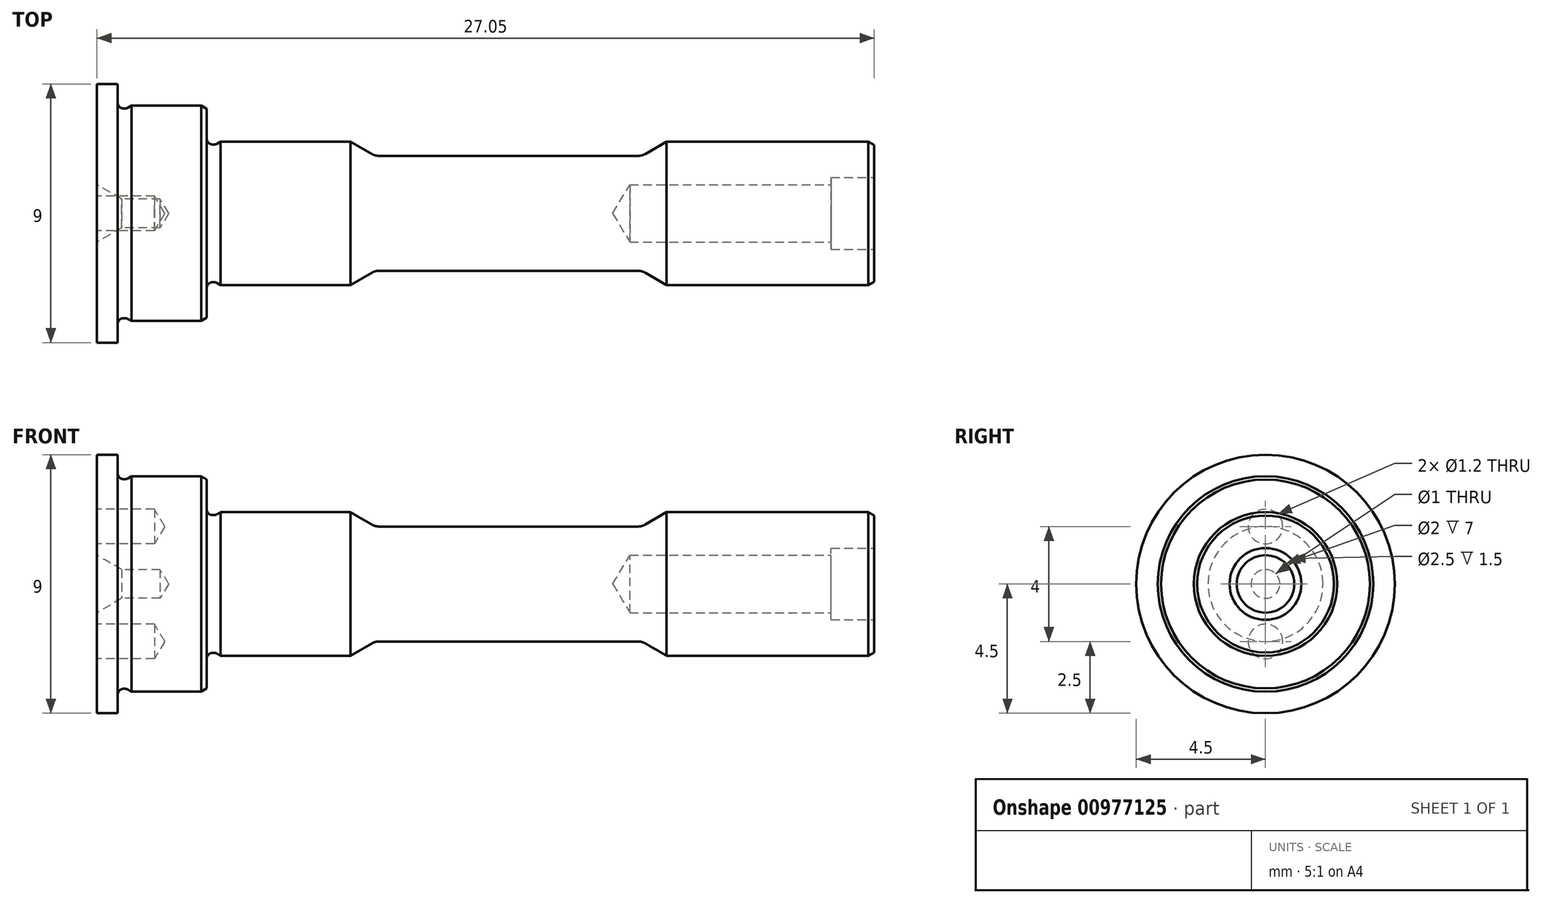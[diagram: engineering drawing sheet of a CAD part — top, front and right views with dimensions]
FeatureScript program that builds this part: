
annotation { "Feature Type Name" : "Feature", "Feature Type Description" : "" }
export const myFeature = defineFeature(function(context is Context, id is Id, definition is map)
    precondition{}
    {
        {
            var Q0;
            Q0=qCreatedBy(makeId("Front.planeOp"),FACE);
            var sketch = newSketch(context, id + "F0", { "sketchPlane" : qUnion([Q0])});
            skLineSegment(sketch, "E0", {"start": v(0, 0) * mm, "end": v(0, 4.5) * mm});
            skLineSegment(sketch, "E1", {"start": v(3.82, 3.75) * mm, "end": v(3.82, 2.6) * mm});
            skArc(sketch, "E2", {"start": v(3.82, 2.6) * mm, "mid": v(3.88, 2.45) * mm, "end": v(4.02, 2.4) * mm});
            skLineSegment(sketch, "E3", {"start": v(4.02, 2.4) * mm, "end": v(4.08, 2.4) * mm});
            skArc(sketch, "E4", {"start": v(4.08, 2.4) * mm, "mid": v(4.13, 2.4) * mm, "end": v(4.18, 2.42) * mm});
            skLineSegment(sketch, "E5", {"start": v(4.18, 2.42) * mm, "end": v(4.3, 2.5) * mm});
            skLineSegment(sketch, "E6", {"start": v(4.3, 2.5) * mm, "end": v(27.05, 2.5) * mm});
            skLineSegment(sketch, "E7", {"start": v(27.05, 2.5) * mm, "end": v(27.05, 0) * mm});
            skLineSegment(sketch, "E8", {"start": v(27.05, 0) * mm, "end": v(0, 0) * mm});
            skLineSegment(sketch, "E9", {"start": v(0, 4.5) * mm, "end": v(0.72, 4.5) * mm});
            skLineSegment(sketch, "E10", {"start": v(0.72, 4.5) * mm, "end": v(0.72, 3.85) * mm});
            skLineSegment(sketch, "E11", {"start": v(1.2, 3.75) * mm, "end": v(3.82, 3.75) * mm});
            skLineSegment(sketch, "E12", {"start": v(1.2, 3.75) * mm, "end": v(1.08, 3.68) * mm});
            skLineSegment(sketch, "E13", {"start": v(0.98, 3.65) * mm, "end": v(0.92, 3.65) * mm});
            skPoint(sketch, "E14.visualSharp", {"position": v(0.72, 3.65) * mm});
            skArc(sketch, "E14.filletArc", {"start": v(0.72, 3.85) * mm, "mid": v(0.78, 3.7) * mm, "end": v(0.92, 3.65) * mm});
            skPoint(sketch, "E15.visualSharp", {"position": v(1.03, 3.65) * mm});
            skArc(sketch, "E15.filletArc", {"start": v(0.98, 3.65) * mm, "mid": v(1.03, 3.66) * mm, "end": v(1.08, 3.68) * mm});
            skLineSegment(sketch, "E16", {"start": v(8.82, 2.5) * mm, "end": v(9.68, 2) * mm});
            skLineSegment(sketch, "E17", {"start": v(9.68, 2) * mm, "end": v(18.97, 2) * mm});
            skLineSegment(sketch, "E18", {"start": v(18.97, 2) * mm, "end": v(19.83, 2.5) * mm});
            skLineSegment(sketch, "E19", {"start": v(19.83, 2.5) * mm, "end": v(8.82, 2.5) * mm});
            skSolve(sketch);
        }
        {
            var Q0;
            Q0=makeQuery(id+"F0.imprint","IMPRINT",FACE,{"disambiguationData":[TD([[makeQuery(id+"F0.imprint","IMPRINT",EDGE,{"derivedFrom":sQuery(id+"F0.wireOp",EDGE,"E0")}),-1.0]])]});
            var Q1;
            Q1=sQuery(id+"F0.wireOp",EDGE,"E8");
            revolve(context, id + "F1", {"surfaceOperationType" : NewSurfaceOperationType.NEW, "entities" : qUnion([Q0]), "axis" : qUnion([Q1]), "revolveType" : RevolveType.FULL});
        }
        {
            var Q0;
            Q0=makeQuery(id+"F1.opRevolve","SWEPT_EDGE",EDGE,{"disambiguationData":[OSD([sQuery(id+"F0.wireOp",EDGE,"E16"),sQuery(id+"F0.wireOp",EDGE,"E17")])]});
            var Q1;
            Q1=makeQuery(id+"F1.opRevolve","SWEPT_EDGE",EDGE,{"disambiguationData":[OSD([sQuery(id+"F0.wireOp",EDGE,"E17"),sQuery(id+"F0.wireOp",EDGE,"E18")])]});
            fillet(context, id + "F2", {"entities" : qUnion([Q0, Q1]), "tangentPropagation" : true, "radius" : .5 * mm, "defaultsChanged" : true, "vertexSettings" : [], "allowEdgeOverflow" : false});
        }
        {
            var Q0;
            Q0=makeQuery(id+"F1.opRevolve","SWEPT_EDGE",EDGE,{"disambiguationData":[OSD([sQuery(id+"F0.wireOp",EDGE,"E1"),sQuery(id+"F0.wireOp",EDGE,"E11")])]});
            var Q1;
            Q1=makeQuery(id+"F1.opRevolve","SWEPT_EDGE",EDGE,{"disambiguationData":[OSD([sQuery(id+"F0.wireOp",EDGE,"E6"),sQuery(id+"F0.wireOp",EDGE,"E7")])]});
            chamfer(context, id + "F3", {"entities" : qUnion([Q0, Q1]), "chamferType" : ChamferType.OFFSET_ANGLE, "width" : .2 * mm, "oppositeDirection" : true, "angle" : 30 * degree, "tangentPropagation" : true});
        }
        {
            var Q0;
            Q0=makeQuery(id+"F1.opRevolve","SWEPT_FACE",FACE,{"disambiguationData":[OSD([sQuery(id+"F0.wireOp",EDGE,"E7")])]});
            var sketch = newSketch(context, id + "F4", { "sketchPlane" : qUnion([Q0])});
            skPoint(sketch, "E20", {"position": v(0, 0) * mm});
            skSolve(sketch);
        }
        {
            var Q0;
            Q0=makeQuery(id+"F1.opRevolve","SWEPT_FACE",FACE,{"disambiguationData":[OSD([sQuery(id+"F0.wireOp",EDGE,"E0")])]});
            var sketch = newSketch(context, id + "F5", { "sketchPlane" : qUnion([Q0])});
            skPoint(sketch, "E21", {"position": v(0, 0) * mm});
            skPoint(sketch, "E22", {"position": v(0, 2) * mm});
            skPoint(sketch, "E23", {"position": v(0, -2) * mm});
            skSolve(sketch);
        }
        {
            var Q0;
            Q0=sQuery(id+"F5.wireOp",VERTEX,"E22");
            var Q1;
            Q1=sQuery(id+"F5.wireOp",VERTEX,"E23");
            var Q2;
            Q2=makeQuery(id+"F1.opRevolve","SWEPT_BODY",BODY,{"disambiguationData":[OSD([sQuery(id+"F0.wireOp",EDGE,"E0"),sQuery(id+"F0.wireOp",EDGE,"E1"),sQuery(id+"F0.wireOp",EDGE,"E2"),sQuery(id+"F0.wireOp",EDGE,"E3"),sQuery(id+"F0.wireOp",EDGE,"E4"),sQuery(id+"F0.wireOp",EDGE,"E5"),sQuery(id+"F0.wireOp",EDGE,"E6"),sQuery(id+"F0.wireOp",EDGE,"E7"),sQuery(id+"F0.wireOp",EDGE,"E8"),sQuery(id+"F0.wireOp",EDGE,"E9"),sQuery(id+"F0.wireOp",EDGE,"E10"),sQuery(id+"F0.wireOp",EDGE,"E11"),sQuery(id+"F0.wireOp",EDGE,"E12"),sQuery(id+"F0.wireOp",EDGE,"E13"),sQuery(id+"F0.wireOp",EDGE,"E14.filletArc"),sQuery(id+"F0.wireOp",EDGE,"E15.filletArc"),sQuery(id+"F0.wireOp",EDGE,"E16"),sQuery(id+"F0.wireOp",EDGE,"E17"),sQuery(id+"F0.wireOp",EDGE,"E18")])]});
            hole(context, id + "F6", {"style" : HoleStyle.SIMPLE, "endStyle" : HoleEndStyle.BLIND, "holeDiameter" : 1.2 * mm, "majorDiameter" : 5 * mm, "holeDepth" : 2 * mm, "isTappedThrough" : true, "tappedDepth" : 12 * mm, "tapClearance" : 3, "locations" : qUnion([Q0, Q1]), "scope" : qUnion([Q2])});
        }
        {
            var Q0;
            Q0=sQuery(id+"F5.wireOp",VERTEX,"E21");
            var Q1;
            Q1=makeQuery(id+"F1.opRevolve","SWEPT_BODY",BODY,{"disambiguationData":[OSD([sQuery(id+"F0.wireOp",EDGE,"E0"),sQuery(id+"F0.wireOp",EDGE,"E1"),sQuery(id+"F0.wireOp",EDGE,"E2"),sQuery(id+"F0.wireOp",EDGE,"E3"),sQuery(id+"F0.wireOp",EDGE,"E4"),sQuery(id+"F0.wireOp",EDGE,"E5"),sQuery(id+"F0.wireOp",EDGE,"E6"),sQuery(id+"F0.wireOp",EDGE,"E7"),sQuery(id+"F0.wireOp",EDGE,"E8"),sQuery(id+"F0.wireOp",EDGE,"E9"),sQuery(id+"F0.wireOp",EDGE,"E10"),sQuery(id+"F0.wireOp",EDGE,"E11"),sQuery(id+"F0.wireOp",EDGE,"E12"),sQuery(id+"F0.wireOp",EDGE,"E13"),sQuery(id+"F0.wireOp",EDGE,"E14.filletArc"),sQuery(id+"F0.wireOp",EDGE,"E15.filletArc"),sQuery(id+"F0.wireOp",EDGE,"E16"),sQuery(id+"F0.wireOp",EDGE,"E17"),sQuery(id+"F0.wireOp",EDGE,"E18")])]});
            hole(context, id + "F7", {"style" : HoleStyle.C_SINK, "endStyle" : HoleEndStyle.BLIND, "holeDiameter" : 1 * mm, "cSinkDiameter" : 2 * mm, "cSinkAngle" : 60 * degree, "majorDiameter" : 5 * mm, "holeDepth" : 2.2 * mm, "isTappedThrough" : true, "tappedDepth" : 12 * mm, "tapClearance" : 3, "locations" : qUnion([Q0]), "scope" : qUnion([Q1])});
        }
        {
            var Q0;
            Q0=sQuery(id+"F4.wireOp",VERTEX,"E20");
            var Q1;
            Q1=makeQuery(id+"F1.opRevolve","SWEPT_BODY",BODY,{"disambiguationData":[OSD([sQuery(id+"F0.wireOp",EDGE,"E0"),sQuery(id+"F0.wireOp",EDGE,"E1"),sQuery(id+"F0.wireOp",EDGE,"E2"),sQuery(id+"F0.wireOp",EDGE,"E3"),sQuery(id+"F0.wireOp",EDGE,"E4"),sQuery(id+"F0.wireOp",EDGE,"E5"),sQuery(id+"F0.wireOp",EDGE,"E6"),sQuery(id+"F0.wireOp",EDGE,"E7"),sQuery(id+"F0.wireOp",EDGE,"E8"),sQuery(id+"F0.wireOp",EDGE,"E9"),sQuery(id+"F0.wireOp",EDGE,"E10"),sQuery(id+"F0.wireOp",EDGE,"E11"),sQuery(id+"F0.wireOp",EDGE,"E12"),sQuery(id+"F0.wireOp",EDGE,"E13"),sQuery(id+"F0.wireOp",EDGE,"E14.filletArc"),sQuery(id+"F0.wireOp",EDGE,"E15.filletArc"),sQuery(id+"F0.wireOp",EDGE,"E16"),sQuery(id+"F0.wireOp",EDGE,"E17"),sQuery(id+"F0.wireOp",EDGE,"E18")])]});
            hole(context, id + "F8", {"style" : HoleStyle.C_BORE, "endStyle" : HoleEndStyle.BLIND, "holeDiameter" : 2 * mm, "cBoreDiameter" : 2.5 * mm, "cBoreDepth" : 1.5 * mm, "majorDiameter" : 5 * mm, "holeDepth" : 8.5 * mm, "isTappedThrough" : true, "tappedDepth" : 12 * mm, "tapClearance" : 3, "locations" : qUnion([Q0]), "scope" : qUnion([Q1])});
        }
    });
